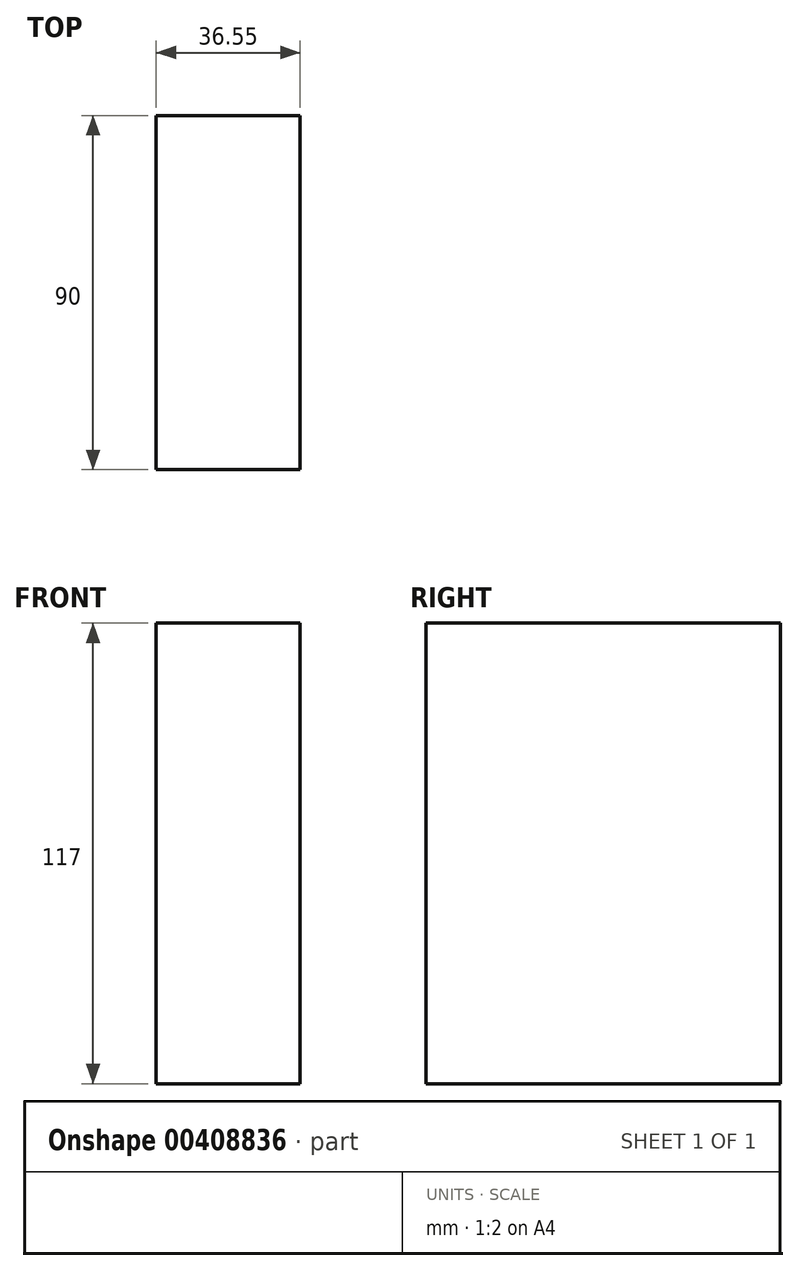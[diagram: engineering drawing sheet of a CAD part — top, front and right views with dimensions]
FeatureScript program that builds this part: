
annotation { "Feature Type Name" : "Feature", "Feature Type Description" : "" }
export const myFeature = defineFeature(function(context is Context, id is Id, definition is map)
    precondition{}
    {
        {
            var Q0;
            Q0=qCreatedBy(makeId("Front.planeOp"),FACE);
            var sketch = newSketch(context, id + "F0", { "sketchPlane" : qUnion([Q0])});
            skLineSegment(sketch, "E0", {"start": v(0, 58.4) * mm, "end": v(36.55, 58.4) * mm});
            skLineSegment(sketch, "E1", {"start": v(36.55, 58.4) * mm, "end": v(36.55, -58.6) * mm});
            skLineSegment(sketch, "E2", {"start": v(0, -58.6) * mm, "end": v(0, 58.4) * mm});
            skLineSegment(sketch, "E3", {"start": v(36.55, -58.6) * mm, "end": v(0, -58.6) * mm});
            skSolve(sketch);
        }
        {
            var Q0;
            Q0 = qSketchRegion(id + "F0", true);
            extrude(context, id + "F1", {"entities" : qUnion([Q0]), "depth" : 90 * mm});
        }
    });
